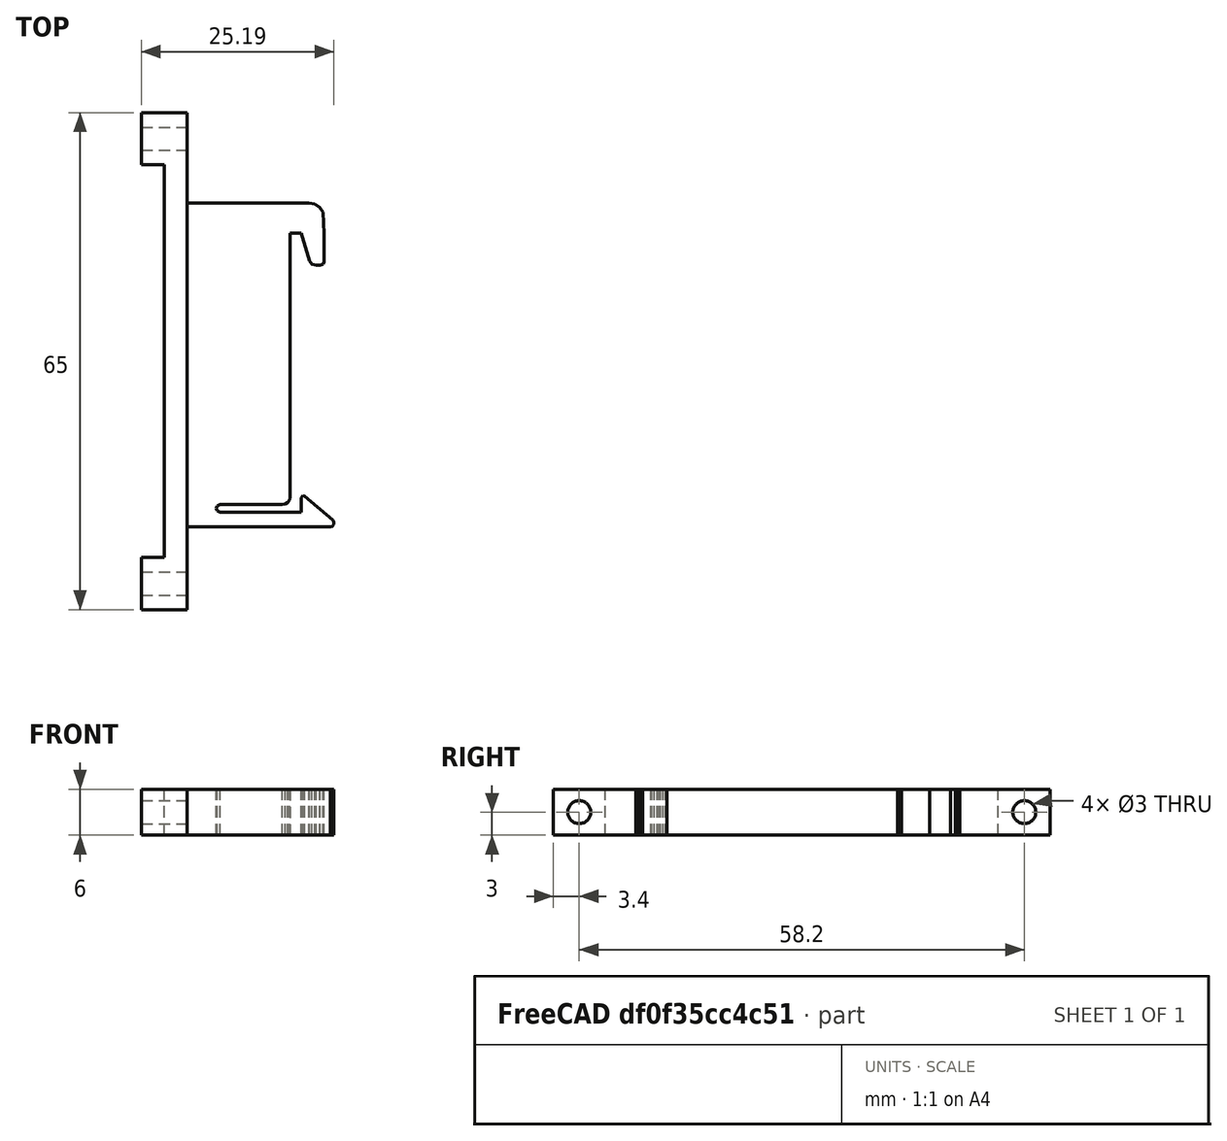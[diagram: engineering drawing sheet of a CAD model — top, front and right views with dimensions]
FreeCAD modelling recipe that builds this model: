
FCSTD DOCUMENT  (FreeCAD 0.18.4R)
Label: 3d-printer-pdb-din-rail-mount
License: All rights reserved
LicenseURL: http://en.wikipedia.org/wiki/All_rights_reserved
objects: Part::Box×4, Part::Feature×3, Part::Cut×3, Part::Cylinder×2, Part::MultiFuse×2, Mesh::Feature×1
note: 14 computed .brp shape members not serialized (recipe doc carries the construction recipe); baked Part::Feature solids carry a one-line shape summary decoded from their .brp

FEATURE [Mesh::Feature] PCB_din_clip
FEATURE [Part::Feature] PCB_din_clip001
  shape: bbox 26.19 x 68.23 x 6 mm, 300 faces, 0 solids (baked)
FEATURE [Part::Box] Box  label="Cube"
  AttacherType = Attacher::AttachEngine3D
  Height = 10
  Length = 10
  Placement = pos=(-10,-38,-3) rot=(0,0,1;0rad)
  Width = 84
FEATURE [Part::Cut] Cut
  Base = -> PCB_din_clip001
  Tool = -> Box
FEATURE [Part::Box] Box001  label="Cube001"
  AttacherType = Attacher::AttachEngine3D
  Height = 6
  Length = 3
  Placement = pos=(-3,-31,-3) rot=(0,0,1;0rad)
  Width = 65
FEATURE [Part::Box] Box002  label="Cube002"
  AttacherType = Attacher::AttachEngine3D
  Height = 6
  Length = 3
  Placement = pos=(-6,27.2,-3) rot=(0,0,1;0rad)
  Width = 6.8
FEATURE [Part::Box] Box003  label="Cube003"
  AttacherType = Attacher::AttachEngine3D
  Height = 6
  Length = 3
  Placement = pos=(-6,-31,-3) rot=(0,0,1;0rad)
  Width = 6.8
FEATURE [Part::Cylinder] Cylinder
  Angle = 360
  AttacherType = Attacher::AttachEngine3D
  Height = 14
  Placement = pos=(-13,-27.6,0) rot=(0,1,0;1.5708rad)
  Radius = 1.5
FEATURE [Part::Cylinder] Cylinder001
  Angle = 360
  AttacherType = Attacher::AttachEngine3D
  Height = 14
  Placement = pos=(-13,30.6,0) rot=(0,1,0;1.5708rad)
  Radius = 1.5
FEATURE [Part::MultiFuse] Fusion
  Shapes = -> [Box001,Box003,Box002]
FEATURE [Part::Cut] Cut001
  Base = -> Fusion
  Tool = -> Cylinder
FEATURE [Part::Cut] Cut002
  Base = -> Cut001
  Tool = -> Cylinder001
FEATURE [Part::Feature] Cut003_solid  label="Cut003 (Solid)"
  shape: bbox 19.19 x 42.37 x 6 mm, 130 faces (baked)
FEATURE [Part::Feature] Cut002001_solid  label="Cut004 (Solid)"
  shape: bbox 6 x 65 x 6 mm, 18 faces (baked)
FEATURE [Part::MultiFuse] Fusion001
  Shapes = -> [Cut003_solid,Cut002001_solid]
